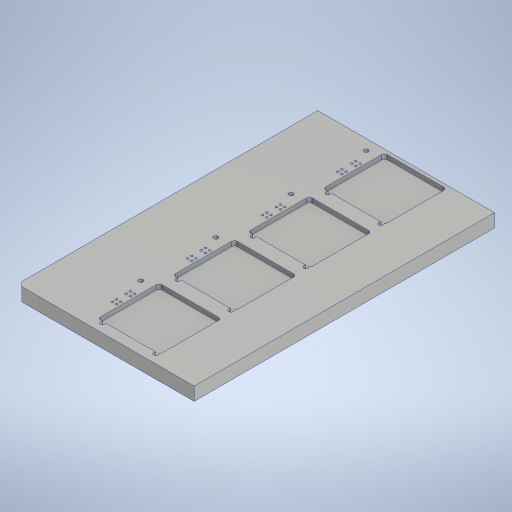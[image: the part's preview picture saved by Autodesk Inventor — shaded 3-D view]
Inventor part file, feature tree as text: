
AUTODESK INVENTOR PART (.ipt)
format: ipt  version: 2023 (Build 270158000, 158)  size: 414,720 bytes
history: native  units: in
note: dims shown in document units (in); Inventor stores cm internally (conversion verified against a paired STEP export)
features: sketch x4, extrude x3, chamfer x1, hole x1
ambient origin geometry x8: Origin, YZ Plane, XZ Plane, XY Plane, X Axis, Y Axis, Z Axis, Center Point
bodies: Solid1 (feature_tree)
feature tree (9):
  extrude  "Extrusion1"  Depth=8.5in
  chamfer  "Chamfer1"  Distance=0.375in
  extrude  "Extrusion10"  Depth=0.125in
  extrude  "Extrusion11"  Depth=0.5in
  hole  "Hole3"  [1 undecoded]
  sketch  "Sketch1"  dims[d0=5.0in d1=8.5in d2=0.375in d3=0.0in]
  sketch  "Sketch12"  dims[d126=0.125in d127=0.125in d128=45.0deg d166=0.125in]
  sketch  "Sketch13"  dims[d167=1.5in d169=0.5in]
  sketch  "Sketch14"  dims[d170=1.5748in d171=1.0in d172=0.0in d194=1.5748in d196=2.125in d197=0.3937in d199=1.0in d221=0.125in d222=0.0in d241=1.752in d242=1.7362in d243=0.0787in d244=1.5748in d246=2.125in d247=0.3937in d249=0.3937in d252=0.0428in d253=0.125in d254=2.1654in d255=0.25in d256=0.125in d257=0.3184in d258=0.1181in d259=0.2756in d260=0.1181in d261=0.0591in d262=0.2362in d263=0.146in d264=0.0787in d265=0.5635in d266=0.315in d267=0.8108in d268=0.0886in d269=0.1181in d270=0.6572in d271=1.5748in d273=2.125in d274=0.3937in d276=0.3937in]
note: 1 required parameter value undecoded (feature->parameter linkage not recoverable at this tier; creation-order binding heuristic only, values carry confidence <= 0.55)
